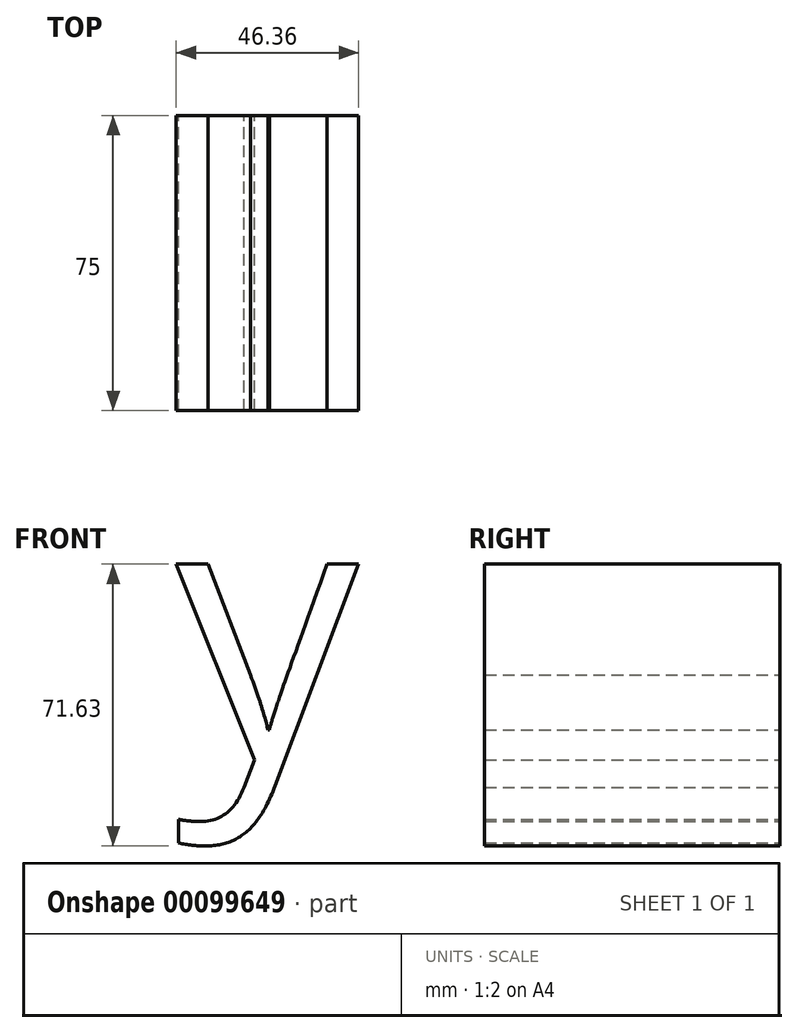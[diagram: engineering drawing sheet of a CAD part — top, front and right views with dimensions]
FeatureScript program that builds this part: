
annotation { "Feature Type Name" : "Feature", "Feature Type Description" : "" }
export const myFeature = defineFeature(function(context is Context, id is Id, definition is map)
    precondition{}
    {
        {
            var Q0;
            Q0=qCreatedBy(makeId("Front.planeOp"),FACE);
            var sketch = newSketch(context, id + "F0", { "sketchPlane" : qUnion([Q0])});
            skText(sketch, "E0", { "text": "noy yaso", "fontName": "OpenSans-Regular.ttf"});
            const initialGuessF0  = {"E0": [-0.12146, -0.02852, 1, 0, 0.0665]};
            skSetInitialGuess(sketch, initialGuessF0);
            skSolve(sketch);
        }
        {
            var Q0;
            Q0=makeQuery(id+"F0.imprint","IMPRINT",FACE,{"disambiguationData":[TD([[makeQuery(id+"F0.imprint","IMPRINT",EDGE,{"derivedFrom":sQuery(id+"F0.wireOp",EDGE,"E0.sketch_text.stroke-34")}),-1.0]])]});
            extrude(context, id + "F1", {"entities" : qUnion([Q0]), "depth" : 75 * mm});
        }
    });
